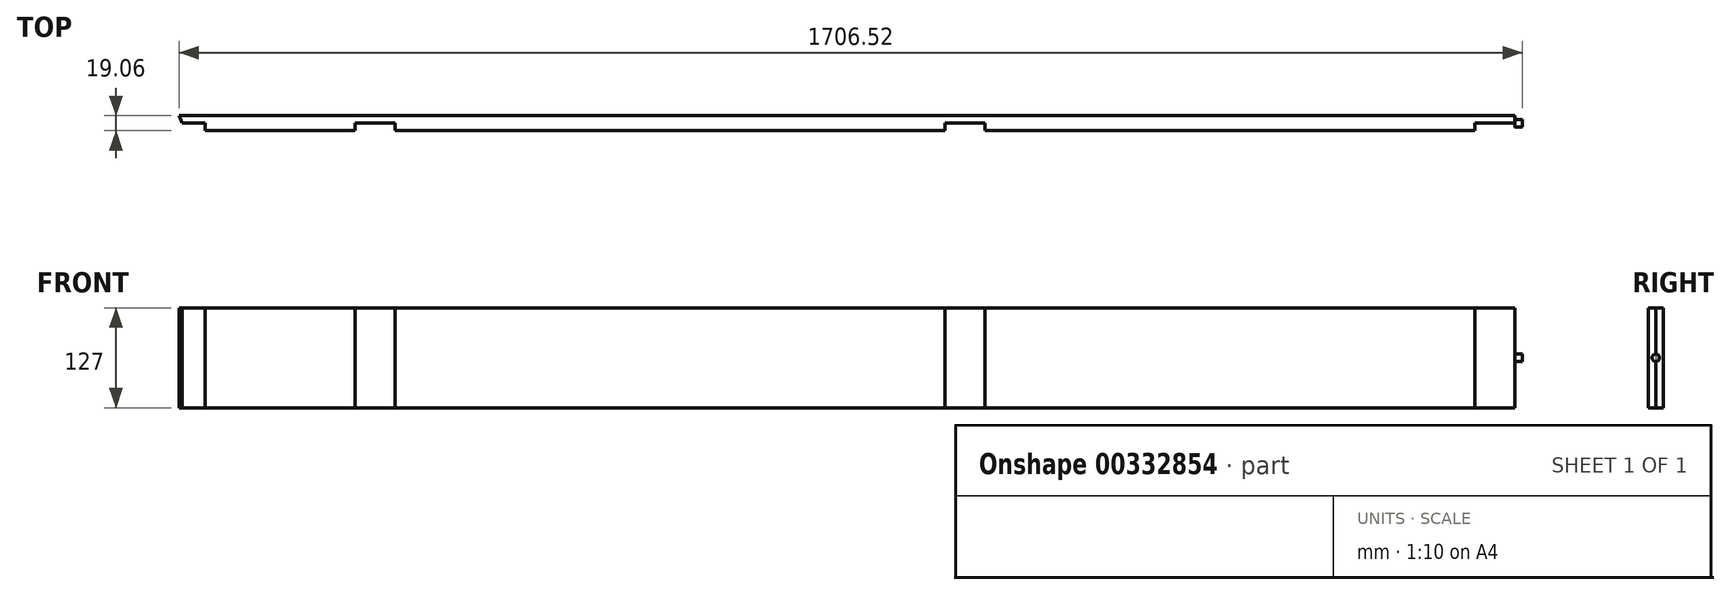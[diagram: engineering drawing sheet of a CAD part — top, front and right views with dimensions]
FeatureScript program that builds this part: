
annotation { "Feature Type Name" : "Feature", "Feature Type Description" : "" }
export const myFeature = defineFeature(function(context is Context, id is Id, definition is map)
    precondition{}
    {
        {
            var Q0;
            Q0=qCreatedBy(makeId("Top.planeOp"),FACE);
            var sketch = newSketch(context, id + "F0", { "sketchPlane" : qUnion([Q0])});
            skLineSegment(sketch, "E0.bottom", {"start": v(-1663.7, -9.52) * mm, "end": v(-1473.2, -9.52) * mm});
            skLineSegment(sketch, "E0.right", {"start": v(0, 0) * mm, "end": v(0, 9.53) * mm});
            skLineSegment(sketch, "E1", {"start": v(-1693.05, 0) * mm, "end": v(-1697, 9.52) * mm});
            skLineSegment(sketch, "E2", {"start": v(0, 9.53) * mm, "end": v(-1697, 9.52) * mm});
            skLineSegment(sketch, "E3.top", {"start": v(-1693.05, 0) * mm, "end": v(-1663.7, 0) * mm});
            skLineSegment(sketch, "E3.right", {"start": v(-1663.7, -9.52) * mm, "end": v(-1663.7, 0) * mm});
            skLineSegment(sketch, "E4.top", {"start": v(-1473.2, 0) * mm, "end": v(-1422.4, 0) * mm});
            skLineSegment(sketch, "E4.left", {"start": v(-1473.2, -9.52) * mm, "end": v(-1473.2, 0) * mm});
            skLineSegment(sketch, "E4.right", {"start": v(-1422.4, -9.52) * mm, "end": v(-1422.4, 0) * mm});
            skLineSegment(sketch, "E5.trimOffspring", {"start": v(-1422.4, -9.52) * mm, "end": v(-723.9, -9.52) * mm});
            skLineSegment(sketch, "E6.top", {"start": v(-723.9, 0) * mm, "end": v(-673.1, 0) * mm});
            skLineSegment(sketch, "E6.left", {"start": v(-723.9, -9.52) * mm, "end": v(-723.9, 0) * mm});
            skLineSegment(sketch, "E6.right", {"start": v(-673.1, -9.52) * mm, "end": v(-673.1, 0) * mm});
            skLineSegment(sketch, "E7.trimOffspring", {"start": v(-673.1, -9.52) * mm, "end": v(-50.8, -9.52) * mm});
            skLineSegment(sketch, "E8.top", {"start": v(-50.8, 0) * mm, "end": v(0, 0) * mm});
            skLineSegment(sketch, "E8.left", {"start": v(-50.8, -9.52) * mm, "end": v(-50.8, 0) * mm});
            skPoint(sketch, "E9.orphan", {"position": v(0, -9.52) * mm});
            skSolve(sketch);
        }
        {
            var Q0;
            Q0=qSketchRegion(id+"F0",true);
            extrude(context, id + "F1", {"entities" : qUnion([Q0]), "endBound" : BoundingType.SYMMETRIC, "depth" : 127 * mm});
        }
        {
            var Q0;
            Q0=qCreatedBy(makeId("Right.planeOp"),FACE);
            var sketch = newSketch(context, id + "F2", { "sketchPlane" : qUnion([Q0])});
            skCircle(sketch, "E10", {"center": v(0, 0) * mm, "radius": 4.76 * mm});
            skSolve(sketch);
        }
        {
            var Q0;
            Q0=qSketchRegion(id+"F2",true);
            extrude(context, id + "F3", {"entities" : qUnion([Q0]), "operationType" : NewBodyOperationType.ADD, "depth" : 9.52 * mm});
        }
    });
